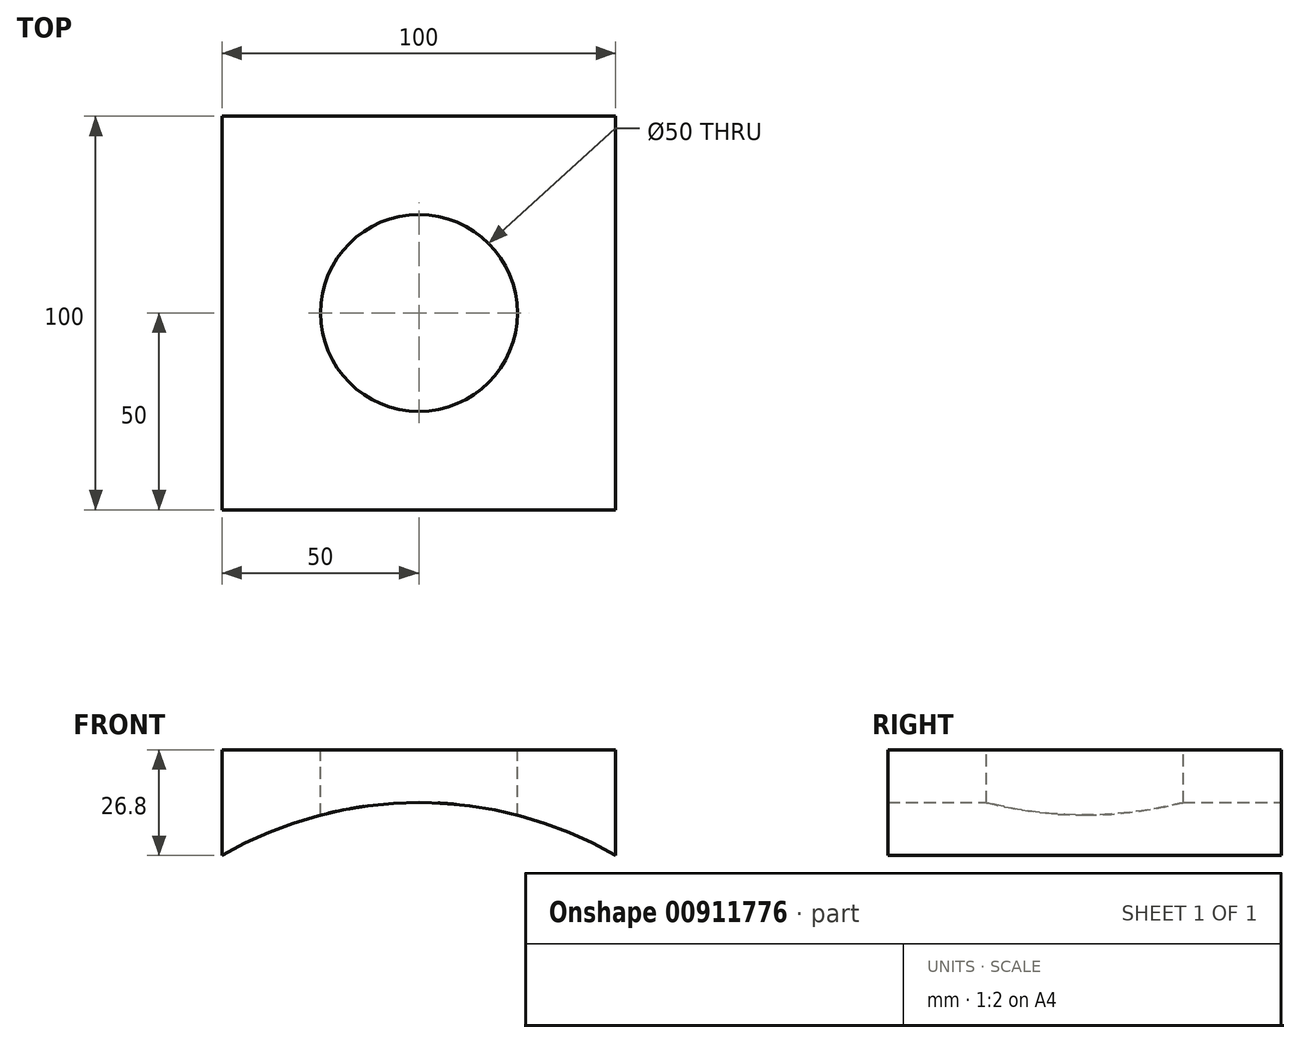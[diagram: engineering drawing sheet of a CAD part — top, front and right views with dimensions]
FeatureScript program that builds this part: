
annotation { "Feature Type Name" : "Feature", "Feature Type Description" : "" }
export const myFeature = defineFeature(function(context is Context, id is Id, definition is map)
    precondition{}
    {
        {
            var Q0;
            Q0=qCreatedBy(makeId("Front.planeOp"),FACE);
            var sketch = newSketch(context, id + "F0", { "sketchPlane" : qUnion([Q0])});
            skLineSegment(sketch, "E0.bottom", {"start": v(50, -13.4) * mm, "end": v(-50, -13.4) * mm});
            skLineSegment(sketch, "E0.top", {"start": v(50, 13.4) * mm, "end": v(-50, 13.4) * mm});
            skLineSegment(sketch, "E0.left", {"start": v(50, -13.4) * mm, "end": v(50, 13.4) * mm});
            skLineSegment(sketch, "E0.right", {"start": v(-50, -13.4) * mm, "end": v(-50, 13.4) * mm});
            skPoint(sketch, "E0.middle", {"position": v(0, 0) * mm});
            skCircle(sketch, "E1", {"center": v(0, -100) * mm, "radius": 100 * mm});
            skSolve(sketch);
        }
        {
            var Q0;
            Q0=makeQuery(id+"F0.imprint","IMPRINT",FACE,{"disambiguationData":[TD([[makeQuery(id+"F0.imprint","IMPRINT",EDGE,{"derivedFrom":sQuery(id+"F0.wireOp",EDGE,"E0.top")}),1.0]])]});
            extrude(context, id + "F1", {"entities" : qUnion([Q0]), "depth" : 100 * mm, "offsetDistance" : 25 * mm});
        }
        {
            var Q0;
            Q0=makeQuery(id+"F1.opExtrude","SWEPT_FACE",FACE,{"disambiguationData":[OSD([sQuery(id+"F0.wireOp",EDGE,"E0.top")])]});
            var sketch = newSketch(context, id + "F2", { "sketchPlane" : qUnion([Q0])});
            skLineSegment(sketch, "E2", {"start": v(-50, 0) * mm, "end": v(50, -100) * mm});
            skLineSegment(sketch, "E3", {"start": v(-50, -100) * mm, "end": v(50, 0) * mm});
            skPoint(sketch, "E4", {"position": v(0, -50) * mm});
            skPoint(sketch, "E4.positionSnap0", {"position": v(0, -50) * mm});
            skSolve(sketch);
        }
        {
            var Q0;
            Q0=sQuery(id+"F2.wireOp",VERTEX,"E4");
            var Q1;
            Q1=makeQuery(id+"F1.opExtrude","SWEPT_BODY",BODY,{"disambiguationData":[OSD([sQuery(id+"F0.wireOp",EDGE,"E0.top"),sQuery(id+"F0.wireOp",EDGE,"E0.left"),sQuery(id+"F0.wireOp",EDGE,"E0.right"),sQuery(id+"F0.wireOp",EDGE,"E1")])]});
            hole(context, id + "F3", {"style" : HoleStyle.SIMPLE, "endStyle" : HoleEndStyle.THROUGH, "holeDiameter" : 50 * mm, "majorDiameter" : 5 * mm, "isTappedThrough" : true, "tappedDepth" : 12 * mm, "tapClearance" : 3, "locations" : qUnion([Q0]), "scope" : qUnion([Q1])});
        }
    });
